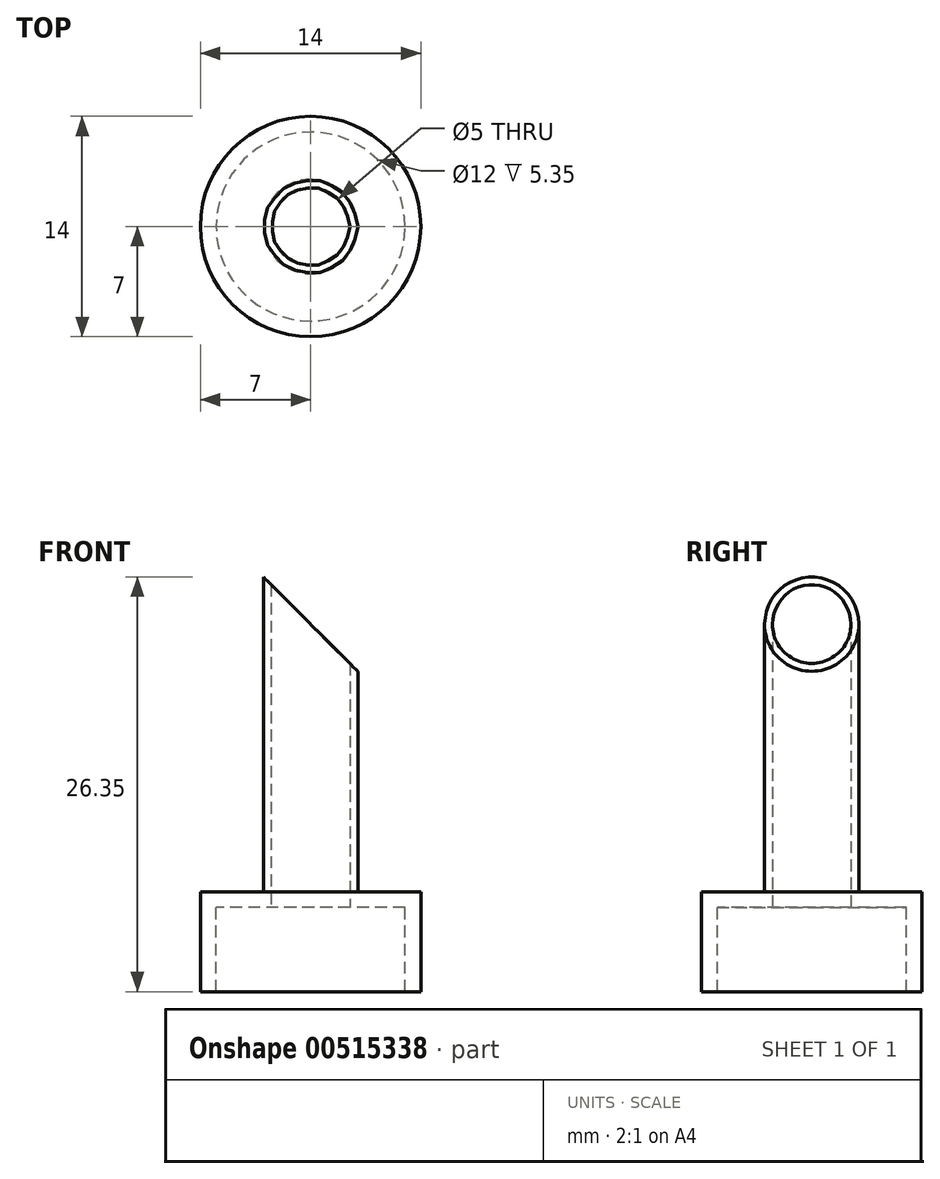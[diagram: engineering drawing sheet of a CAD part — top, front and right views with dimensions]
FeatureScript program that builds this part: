
annotation { "Feature Type Name" : "Feature", "Feature Type Description" : "" }
export const myFeature = defineFeature(function(context is Context, id is Id, definition is map)
    precondition{}
    {
        {
            var Q0;
            Q0=qCreatedBy(makeId("Top.planeOp"),FACE);
            var sketch = newSketch(context, id + "F0", { "sketchPlane" : qUnion([Q0])});
            skCircle(sketch, "E0", {"center": v(0, 0) * mm, "radius": 3 * mm});
            skCircle(sketch, "E1", {"center": v(0, 0) * mm, "radius": 2.5 * mm});
            skSolve(sketch);
        }
        {
            var Q0;
            Q0=makeQuery(id+"F0.imprint","IMPRINT",FACE,{"disambiguationData":[TD([[makeQuery(id+"F0.imprint","IMPRINT",EDGE,{"derivedFrom":sQuery(id+"F0.wireOp",EDGE,"E0")}),1.0]])]});
            extrude(context, id + "F1", {"entities" : qUnion([Q0]), "depth" : 20 * mm, "offsetDistance" : 25.4 * mm});
        }
        {
            var Q0;
            Q0=qCreatedBy(makeId("Top.planeOp"),FACE);
            var sketch = newSketch(context, id + "F2", { "sketchPlane" : qUnion([Q0])});
            skCircle(sketch, "E2", {"center": v(0, 0) * mm, "radius": 7 * mm});
            skCircle(sketch, "E3", {"center": v(0, 0) * mm, "radius": 6 * mm});
            skSolve(sketch);
        }
        {
            var Q0;
            Q0 = qSketchRegion(id + "F2", true);
            extrude(context, id + "F3", {"entities" : qUnion([Q0]), "oppositeDirection" : true, "depth" : 6.35 * mm, "offsetDistance" : 25.4 * mm});
        }
        {
            var Q0;
            Q0=qCreatedBy(makeId("Top.planeOp"),FACE);
            var sketch = newSketch(context, id + "F4", { "sketchPlane" : qUnion([Q0])});
            skCircle(sketch, "E4.0", {"center": v(0, 0) * mm, "radius": 6 * mm});
            skCircle(sketch, "E5.0", {"center": v(0, 0) * mm, "radius": 2.5 * mm});
            skSolve(sketch);
        }
        {
            var Q0;
            Q0 = qSketchRegion(id + "F4", true);
            extrude(context, id + "F5", {"entities" : qUnion([Q0]), "operationType" : NewBodyOperationType.ADD, "oppositeDirection" : true, "depth" : 1 * mm, "offsetDistance" : 25.4 * mm});
        }
        {
            var Q0;
            Q0=qCreatedBy(makeId("Front.planeOp"),FACE);
            var sketch = newSketch(context, id + "F6", { "sketchPlane" : qUnion([Q0])});
            skLineSegment(sketch, "E6.0", {"start": v(-3, 20) * mm, "end": v(3, 20) * mm});
            skLineSegment(sketch, "E7", {"start": v(3, 20) * mm, "end": v(3, 0) * mm});
            skLineSegment(sketch, "E8", {"start": v(-3, 20) * mm, "end": v(3, 14) * mm});
            skSolve(sketch);
        }
        {
            var Q0;
            Q0 = qSketchRegion(id + "F6", true);
            extrude(context, id + "F7", {"entities" : qUnion([Q0]), "operationType" : NewBodyOperationType.REMOVE, "endBound" : BoundingType.SYMMETRIC, "oppositeDirection" : true, "depth" : 25.4 * mm, "offsetDistance" : 25.4 * mm});
        }
    });
